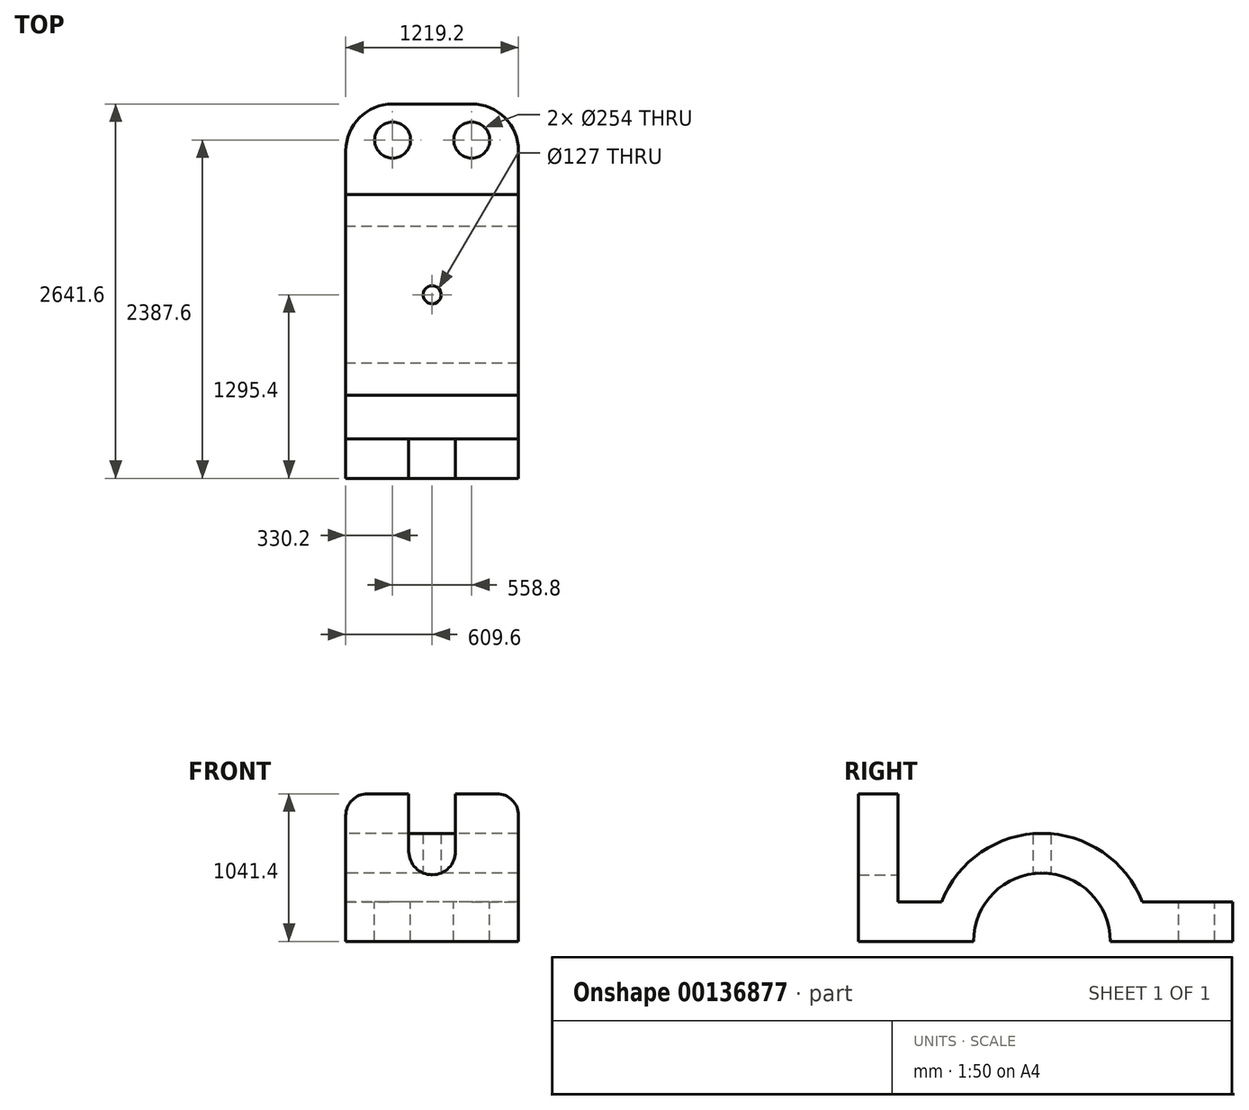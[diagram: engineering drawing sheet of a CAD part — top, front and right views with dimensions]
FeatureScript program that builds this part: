
annotation { "Feature Type Name" : "Feature", "Feature Type Description" : "" }
export const myFeature = defineFeature(function(context is Context, id is Id, definition is map)
    precondition{}
    {
        {
            var Q0;
            Q0=qCreatedBy(makeId("Front.planeOp"),FACE);
            var sketch = newSketch(context, id + "F0", { "sketchPlane" : qUnion([Q0])});
            skLineSegment(sketch, "E0", {"start": v(0, 0) * mm, "end": v(609.6, 0) * mm});
            skLineSegment(sketch, "E1", {"start": v(0, 0) * mm, "end": v(-609.6, 0) * mm});
            skLineSegment(sketch, "E2", {"start": v(-609.6, 0) * mm, "end": v(-609.6, 889) * mm});
            skLineSegment(sketch, "E3", {"start": v(609.6, 0) * mm, "end": v(609.6, 889) * mm});
            skArc(sketch, "E4", {"start": v(-165.1, 635) * mm, "mid": v(0, 469.9) * mm, "end": v(165.1, 635) * mm});
            skLineSegment(sketch, "E5", {"start": v(165.1, 635) * mm, "end": v(165.1, 1041.4) * mm});
            skLineSegment(sketch, "E6", {"start": v(165.1, 1041.4) * mm, "end": v(457.2, 1041.4) * mm});
            skLineSegment(sketch, "E7", {"start": v(-165.1, 635) * mm, "end": v(-165.1, 1041.4) * mm});
            skLineSegment(sketch, "E8", {"start": v(-165.1, 1041.4) * mm, "end": v(-457.2, 1041.4) * mm});
            skPoint(sketch, "E9.visualSharp", {"position": v(-609.6, 1041.4) * mm});
            skArc(sketch, "E9.filletArc", {"start": v(-457.2, 1041.4) * mm, "mid": v(-564.96, 996.76) * mm, "end": v(-609.6, 889) * mm});
            skPoint(sketch, "E10.visualSharp", {"position": v(609.6, 1041.4) * mm});
            skArc(sketch, "E10.filletArc", {"start": v(609.6, 889) * mm, "mid": v(564.96, 996.76) * mm, "end": v(457.2, 1041.4) * mm});
            skSolve(sketch);
        }
        {
            var Q0;
            Q0=qSketchRegion(id+"F0",true);
            extrude(context, id + "F1", {"entities" : qUnion([Q0]), "depth" : 279.4 * mm});
        }
        {
            var Q0;
            Q0=qCreatedBy(makeId("Right.planeOp"),FACE);
            var sketch = newSketch(context, id + "F2", { "sketchPlane" : qUnion([Q0])});
            skLineSegment(sketch, "E11", {"start": v(0, 0) * mm, "end": v(533.78, 0) * mm});
            skArc(sketch, "E12", {"start": v(1498.22, 0) * mm, "mid": v(1016, 482.22) * mm, "end": v(533.78, 0) * mm});
            skArc(sketch, "E13", {"start": v(1724.93, 279.4) * mm, "mid": v(1016, 762) * mm, "end": v(307.07, 279.4) * mm});
            skLineSegment(sketch, "E14", {"start": v(2362.2, 0) * mm, "end": v(2362.2, 279.4) * mm});
            skLineSegment(sketch, "E15", {"start": v(2362.2, 279.4) * mm, "end": v(1724.93, 279.4) * mm});
            skLineSegment(sketch, "E16.trimOffspring", {"start": v(307.07, 279.4) * mm, "end": v(0, 279.4) * mm});
            skLineSegment(sketch, "E17.trimOffspring", {"start": v(1498.22, 0) * mm, "end": v(2362.2, 0) * mm});
            skLineSegment(sketch, "E18", {"start": v(0, 279.4) * mm, "end": v(0, 0) * mm});
            skSolve(sketch);
        }
        {
            var Q0;
            Q0=qSketchRegion(id+"F2",true);
            extrude(context, id + "F3", {"entities" : qUnion([Q0]), "operationType" : NewBodyOperationType.ADD, "endBound" : BoundingType.SYMMETRIC, "depth" : 1219.2 * mm});
        }
        {
            var Q0;
            Q0=makeQuery(id+"F3.opExtrude","SWEPT_FACE",FACE,{"disambiguationData":[OSD([sQuery(id+"F2.wireOp",EDGE,"E15")])]});
            var sketch = newSketch(context, id + "F4", { "sketchPlane" : qUnion([Q0])});
            skPoint(sketch, "E19.endSnap0", {"position": v(0, 1724.93) * mm});
            skCircle(sketch, "E20", {"center": v(279.4, 2108.2) * mm, "radius": 127 * mm});
            skCircle(sketch, "E21", {"center": v(-279.4, 2108.2) * mm, "radius": 127 * mm});
            skLineSegment(sketch, "E22", {"start": v(0, 0) * mm, "end": v(0, 1016) * mm});
            skCircle(sketch, "E23", {"center": v(0, 1016) * mm, "radius": 63.5 * mm});
            skSolve(sketch);
        }
        {
            var Q0;
            Q0=qSketchRegion(id+"F4",true);
            extrude(context, id + "F5", {"entities" : qUnion([Q0]), "operationType" : NewBodyOperationType.REMOVE, "endBound" : BoundingType.THROUGH_ALL, "oppositeDirection" : true, "depth" : 25.4 * mm});
        }
        {
            var Q0;
            Q0=qSketchRegion(id+"F4",true);
            extrude(context, id + "F6", {"entities" : qUnion([Q0]), "operationType" : NewBodyOperationType.REMOVE, "endBound" : BoundingType.THROUGH_ALL, "depth" : 25.4 * mm});
        }
        {
            var Q0;
            Q0=makeQuery(id+"F3.opExtrude","CAP_EDGE",EDGE,{"disambiguationData":[OSD([sQuery(id+"F2.wireOp",EDGE,"E14")])],"isStart":true});
            var Q1;
            Q1=makeQuery(id+"F3.opExtrude","CAP_EDGE",EDGE,{"disambiguationData":[OSD([sQuery(id+"F2.wireOp",EDGE,"E14")])],"isStart":false});
            fillet(context, id + "F7", {"entities" : qUnion([Q0, Q1]), "radius" : 330.2 * mm, "tangentPropagation" : true, "allowEdgeOverflow" : false});
        }
    });
